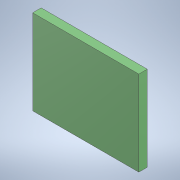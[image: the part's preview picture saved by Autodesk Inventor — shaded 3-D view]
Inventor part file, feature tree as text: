
AUTODESK INVENTOR PART (.ipt)
format: ipt  version: 2021 (Build 250183000, 183)  size: 95,744 bytes
history: native  units: mm
features: other x1, extrude x1, sketch x1
ambient origin geometry x8: Origin, YZ Plane, XZ Plane, XY Plane, X Axis, Y Axis, Z Axis, Center Point
bodies: Body1 (feature_tree)
feature tree (3):
  other  "Sólido1"
  extrude  "Extrusão1"  Depth=250.0mm
  sketch  "Esboço1"  dims[d0=200.0mm d1=250.0mm d2=20.0mm d3=0.0mm]
